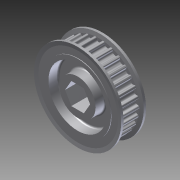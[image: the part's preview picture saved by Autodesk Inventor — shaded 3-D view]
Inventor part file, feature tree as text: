
AUTODESK INVENTOR PART (.ipt)
format: ipt  version: 2014 SP1 (Build 180222100, 222)  size: 1,243,136 bytes
history: native  units: in
note: dims shown in document units (in); Inventor stores cm internally (conversion verified against a paired STEP export)
features: mirror x1, other x1, imported_body x1
ambient origin geometry x8: Origin, YZ Plane, XZ Plane, XY Plane, X Axis, Y Axis, Z Axis, Center Point
bodies: Body1 (feature_tree)
feature tree (3):
  mirror  "Mirror1"
  other  "217-3229-STEP1"
  imported_body  "Base1"
